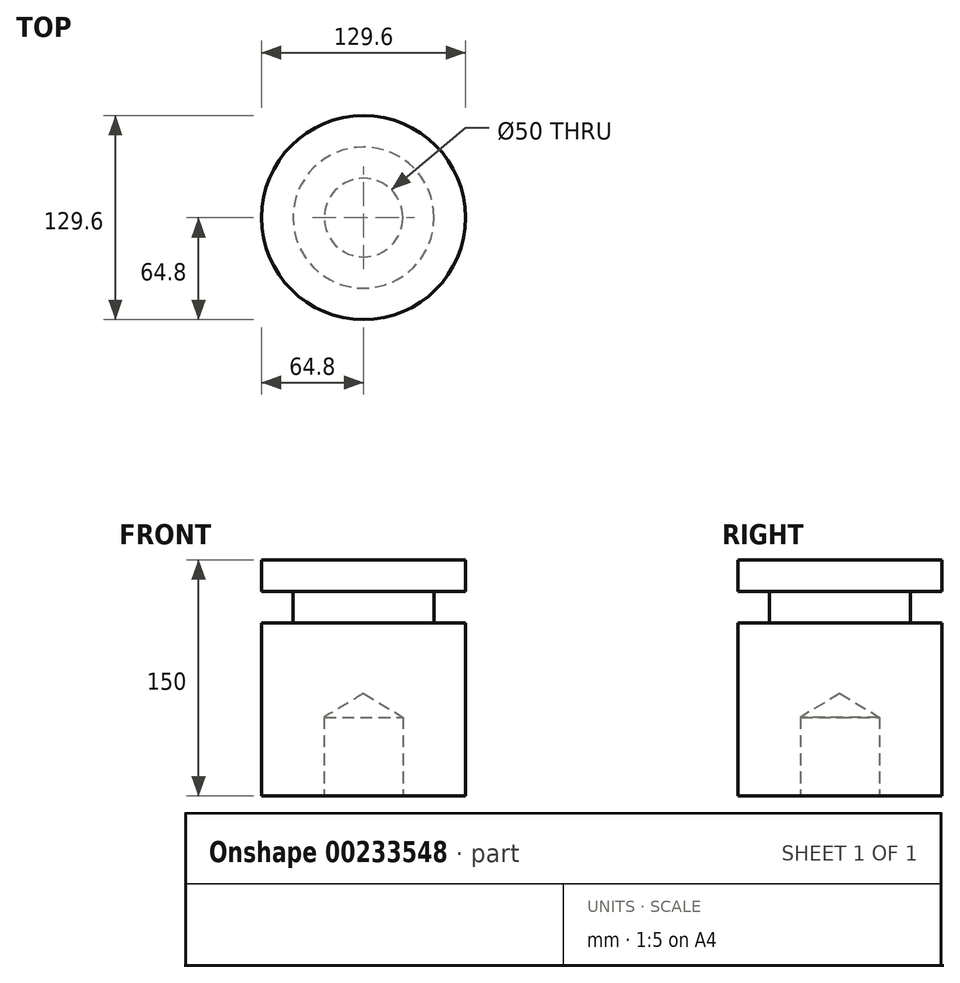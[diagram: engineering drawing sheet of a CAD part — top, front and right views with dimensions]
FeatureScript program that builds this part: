
annotation { "Feature Type Name" : "Feature", "Feature Type Description" : "" }
export const myFeature = defineFeature(function(context is Context, id is Id, definition is map)
    precondition{}
    {
        {
            var Q0;
            Q0=qCreatedBy(makeId("Front.planeOp"),FACE);
            var sketch = newSketch(context, id + "F0", { "sketchPlane" : qUnion([Q0])});
            skLineSegment(sketch, "E0", {"start": v(0, 0) * mm, "end": v(-64.8, 0) * mm});
            skLineSegment(sketch, "E1", {"start": v(-64.8, 0) * mm, "end": v(-64.8, 110) * mm});
            skLineSegment(sketch, "E2", {"start": v(-64.8, 110) * mm, "end": v(-44.8, 110) * mm});
            skLineSegment(sketch, "E3", {"start": v(-44.8, 110) * mm, "end": v(-44.8, 130) * mm});
            skLineSegment(sketch, "E4", {"start": v(-44.8, 130) * mm, "end": v(-64.8, 130) * mm});
            skLineSegment(sketch, "E5", {"start": v(-64.8, 130) * mm, "end": v(-64.8, 150) * mm});
            skLineSegment(sketch, "E6", {"start": v(-64.8, 150) * mm, "end": v(0, 150) * mm});
            skLineSegment(sketch, "E7", {"start": v(0, 150) * mm, "end": v(0, 0) * mm});
            skSolve(sketch);
        }
        {
            var Q0;
            Q0=makeQuery(id+"F0.imprint","IMPRINT",FACE,{"disambiguationData":[TD([[makeQuery(id+"F0.imprint","IMPRINT",EDGE,{"derivedFrom":sQuery(id+"F0.wireOp",EDGE,"E0")}),-1.0]])]});
            var Q1;
            Q1=sQuery(id+"F0.wireOp",EDGE,"E7");
            revolve(context, id + "F1", {"entities" : qUnion([Q0]), "axis" : qUnion([Q1]), "revolveType" : RevolveType.FULL});
        }
        {
            var Q0;
            Q0=makeQuery(id+"F1.opRevolve","SWEPT_FACE",FACE,{"disambiguationData":[OSD([sQuery(id+"F0.wireOp",EDGE,"E0")])]});
            var sketch = newSketch(context, id + "F2", { "sketchPlane" : qUnion([Q0])});
            skCircle(sketch, "E8", {"center": v(0, 0) * mm, "radius": 25 * mm, "construction": true});
            skSolve(sketch);
        }
        {
            var Q0;
            Q0=sQuery(id+"F2.wireOp",VERTEX,"E8.center");
            var Q1;
            Q1=makeQuery(id+"F1.opRevolve","SWEPT_BODY",BODY,{"disambiguationData":[OSD([sQuery(id+"F0.wireOp",EDGE,"E0"),sQuery(id+"F0.wireOp",EDGE,"E1"),sQuery(id+"F0.wireOp",EDGE,"E2"),sQuery(id+"F0.wireOp",EDGE,"E3"),sQuery(id+"F0.wireOp",EDGE,"E4"),sQuery(id+"F0.wireOp",EDGE,"E5"),sQuery(id+"F0.wireOp",EDGE,"E6"),sQuery(id+"F0.wireOp",EDGE,"E7")])]});
            hole(context, id + "F3", {"style" : HoleStyle.SIMPLE, "endStyle" : HoleEndStyle.BLIND, "holeDiameter" : 50 * mm, "holeDepth" : 50 * mm, "startFromSketch" : true, "locations" : qUnion([Q0]), "scope" : qUnion([Q1])});
        }
    });
